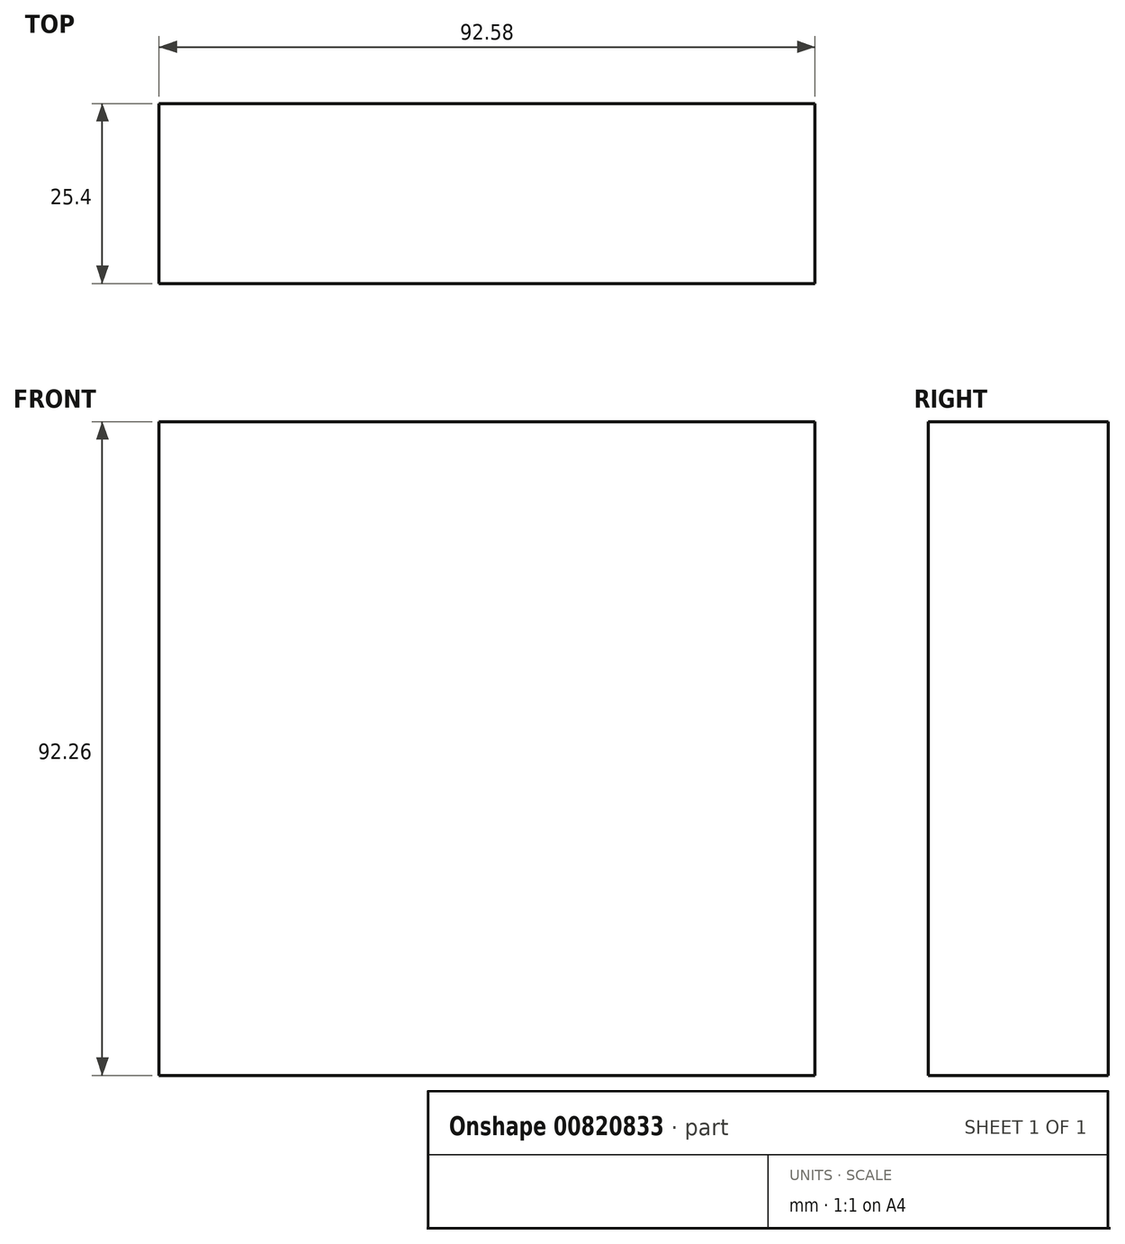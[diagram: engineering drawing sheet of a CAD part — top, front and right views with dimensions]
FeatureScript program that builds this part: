
annotation { "Feature Type Name" : "Feature", "Feature Type Description" : "" }
export const myFeature = defineFeature(function(context is Context, id is Id, definition is map)
    precondition{}
    {
        {
            var Q0;
            Q0=qCreatedBy(makeId("Front.planeOp"),FACE);
            var sketch = newSketch(context, id + "F0", { "sketchPlane" : qUnion([Q0])});
            skLineSegment(sketch, "E0.bottom", {"start": v(-99.56, 25.9) * mm, "end": v(-6.98, 25.9) * mm});
            skLineSegment(sketch, "E0.top", {"start": v(-99.56, -66.37) * mm, "end": v(-6.98, -66.37) * mm});
            skLineSegment(sketch, "E0.left", {"start": v(-99.56, 25.9) * mm, "end": v(-99.56, -66.37) * mm});
            skLineSegment(sketch, "E0.right", {"start": v(-6.98, 25.9) * mm, "end": v(-6.98, -66.37) * mm});
            skSolve(sketch);
        }
        {
            var Q0;
            Q0 = qSketchRegion(id + "F0", true);
            extrude(context, id + "F1", {"entities" : qUnion([Q0]), "depth" : 25.4 * mm, "offsetDistance" : 25.4 * mm});
        }
    });
